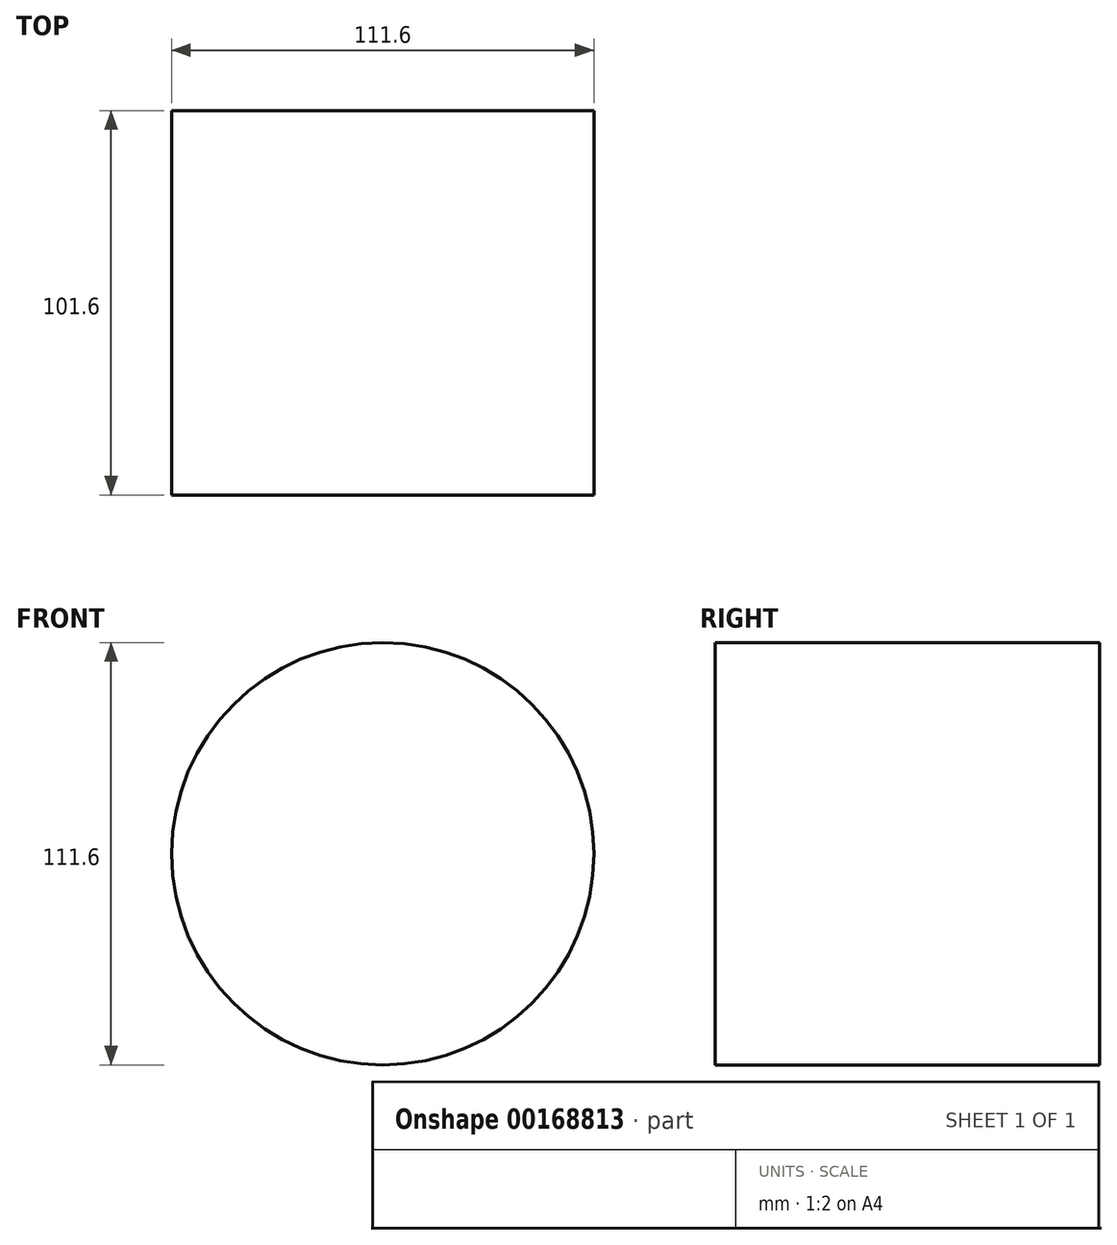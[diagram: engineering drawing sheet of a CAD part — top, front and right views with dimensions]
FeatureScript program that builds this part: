
annotation { "Feature Type Name" : "Feature", "Feature Type Description" : "" }
export const myFeature = defineFeature(function(context is Context, id is Id, definition is map)
    precondition{}
    {
        {
            var Q0;
            Q0=qCreatedBy(makeId("Front.planeOp"),FACE);
            var sketch = newSketch(context, id + "F0", { "sketchPlane" : qUnion([Q0])});
            skCircle(sketch, "E0", {"center": v(0, 0) * mm, "radius": 55.8 * mm});
            skSolve(sketch);
        }
        {
            var Q0;
            Q0 = qSketchRegion(id + "F0", true);
            var Q1;
            Q1=makeQuery(id+"F0.imprint","IMPRINT",FACE,{"disambiguationData":[TD([[makeQuery(id+"F0.imprint","IMPRINT",EDGE,{"derivedFrom":sQuery(id+"F0.wireOp",EDGE,"E0")}),1.0]])]});
            extrude(context, id + "F1", {"entities" : qUnion([Q0, Q1]), "depth" : 101.6 * mm});
        }
    });
